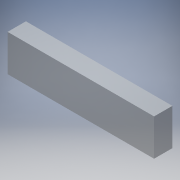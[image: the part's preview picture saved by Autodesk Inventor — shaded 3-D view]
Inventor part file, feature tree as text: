
AUTODESK INVENTOR PART (.ipt)
format: ipt  version: 2018.1 (Build 221171000, 171)  size: 92,672 bytes
history: native  units: mm
features: extrude x1, sketch x1
ambient origin geometry x8: Origin, YZ Plane, XZ Plane, XY Plane, X Axis, Y Axis, Z Axis, Center Point
bodies: Solid1 (feature_tree)
feature tree (2):
  extrude  "Extrusion1"  Depth=200.0mm
  sketch  "Sketch1"  dims[d0=100.0mm d1=0.0mm d2=200.0mm d3=600.0mm]
